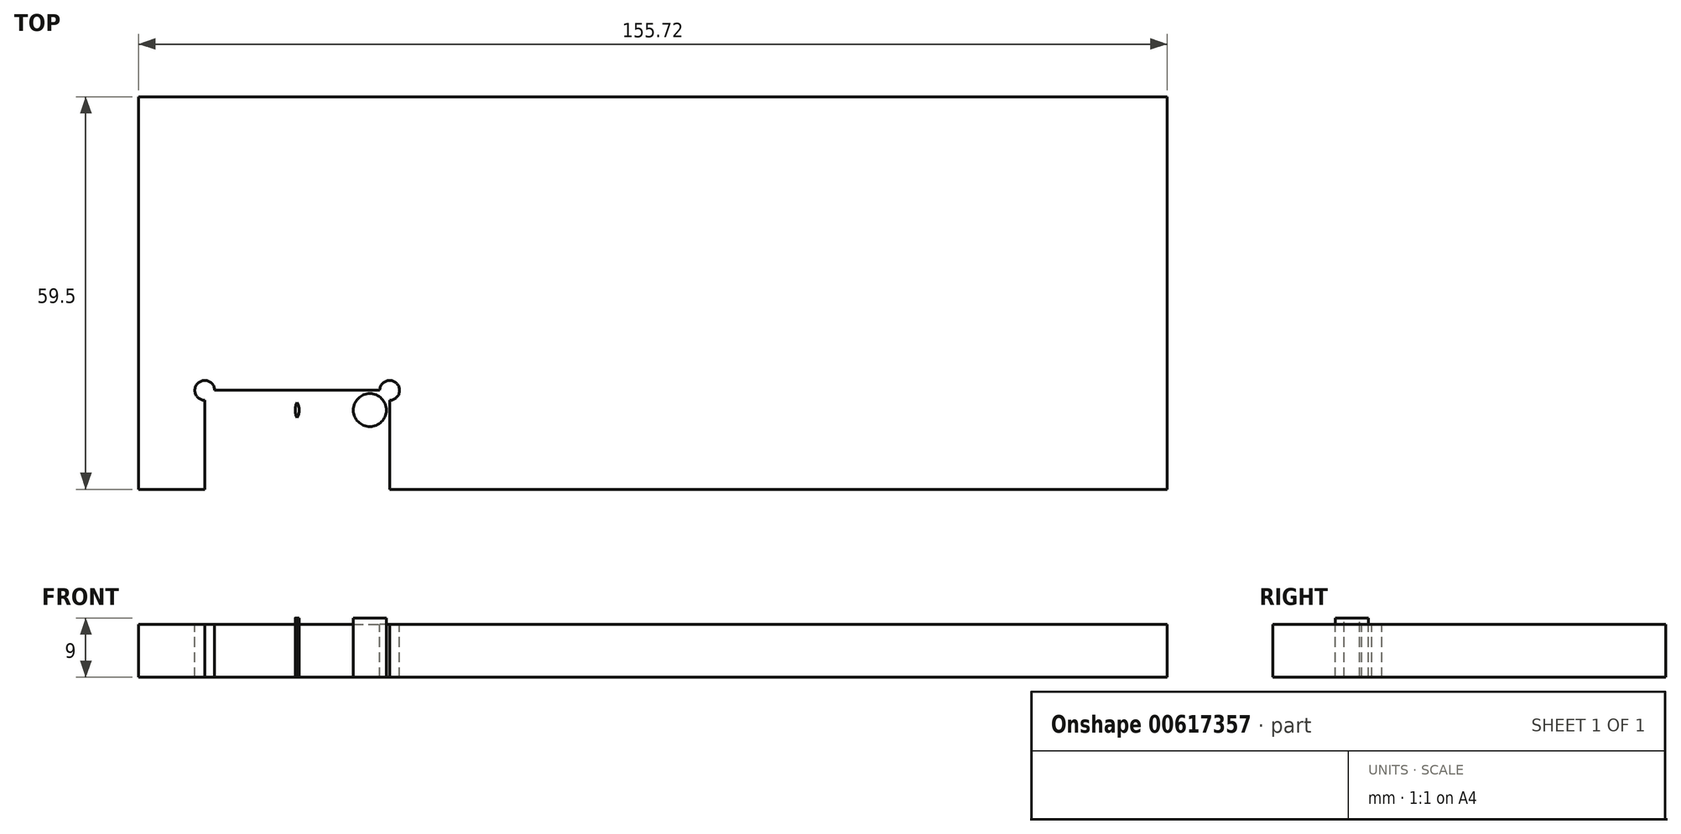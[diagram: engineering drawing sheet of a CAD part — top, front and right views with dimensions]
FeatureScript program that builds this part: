
annotation { "Feature Type Name" : "Feature", "Feature Type Description" : "" }
export const myFeature = defineFeature(function(context is Context, id is Id, definition is map)
    precondition{}
    {
        {
            var Q0;
            Q0=qCreatedBy(makeId("Top.planeOp"),FACE);
            var sketch = newSketch(context, id + "F0", { "sketchPlane" : qUnion([Q0])});
            skLineSegment(sketch, "E0.bottom", {"start": v(77.86, 29.75) * mm, "end": v(-77.86, 29.75) * mm});
            skLineSegment(sketch, "E0.top", {"start": v(77.86, -29.75) * mm, "end": v(-39.86, -29.75) * mm});
            skLineSegment(sketch, "E0.left", {"start": v(77.86, 29.75) * mm, "end": v(77.86, -29.75) * mm});
            skLineSegment(sketch, "E0.right", {"start": v(-77.86, 29.75) * mm, "end": v(-77.86, -29.75) * mm});
            skPoint(sketch, "E0.middle", {"position": v(0, 0) * mm});
            skLineSegment(sketch, "E1", {"start": v(-67.86, -29.75) * mm, "end": v(-67.86, -16.25) * mm});
            skLineSegment(sketch, "E2", {"start": v(-66.36, -14.75) * mm, "end": v(-41.36, -14.75) * mm});
            skLineSegment(sketch, "E3", {"start": v(-39.86, -16.25) * mm, "end": v(-39.86, -29.75) * mm});
            skArc(sketch, "E4", {"start": v(-39.86, -16.25) * mm, "mid": v(-38.8, -13.69) * mm, "end": v(-41.36, -14.75) * mm});
            skArc(sketch, "E5", {"start": v(-66.36, -14.75) * mm, "mid": v(-68.92, -13.69) * mm, "end": v(-67.86, -16.25) * mm});
            skLineSegment(sketch, "E6.trimOffspring", {"start": v(-67.86, -29.75) * mm, "end": v(-77.86, -29.75) * mm});
            skLineSegment(sketch, "E7", {"start": v(-67.86, -29.75) * mm, "end": v(-39.86, -29.75) * mm});
            skSolve(sketch);
        }
        {
            var Q0;
            Q0=makeQuery(id+"F0.imprint","IMPRINT",FACE,{"disambiguationData":[TD([[makeQuery(id+"F0.imprint","IMPRINT",EDGE,{"derivedFrom":sQuery(id+"F0.wireOp",EDGE,"E0.bottom")}),1.0]])]});
            var Q1;
            Q1=makeQuery(id+"F0.imprint","IMPRINT",FACE,{"disambiguationData":[TD([[makeQuery(id+"F0.imprint","IMPRINT",EDGE,{"derivedFrom":sQuery(id+"F0.wireOp",EDGE,"E1")}),-1.0]])]});
            extrude(context, id + "F1", {"entities" : qUnion([Q0, Q1]), "depth" : 8 * mm, "offsetDistance" : 25 * mm});
        }
        {
            var Q0;
            Q0=makeQuery(id+"F1.opExtrude","CAP_FACE",FACE,{"disambiguationData":[OSD([sQuery(id+"F0.wireOp",EDGE,"E0.bottom"),sQuery(id+"F0.wireOp",EDGE,"E0.top"),sQuery(id+"F0.wireOp",EDGE,"E0.left"),sQuery(id+"F0.wireOp",EDGE,"E0.right"),sQuery(id+"F0.wireOp",EDGE,"E6.trimOffspring"),sQuery(id+"F0.wireOp",EDGE,"E7")])],"isStart":false});
            var sketch = newSketch(context, id + "F2", { "sketchPlane" : qUnion([Q0])});
            skLineSegment(sketch, "E8", {"start": v(-67.86, -29.75) * mm, "end": v(-67.86, -16.25) * mm});
            skLineSegment(sketch, "E9", {"start": v(-66.36, -14.75) * mm, "end": v(-41.36, -14.75) * mm});
            skLineSegment(sketch, "E10", {"start": v(-39.86, -16.25) * mm, "end": v(-39.86, -29.75) * mm});
            skArc(sketch, "E11", {"start": v(-39.86, -16.25) * mm, "mid": v(-38.8, -13.69) * mm, "end": v(-41.36, -14.75) * mm});
            skArc(sketch, "E12", {"start": v(-66.36, -14.75) * mm, "mid": v(-68.92, -13.69) * mm, "end": v(-67.86, -16.25) * mm});
            skSolve(sketch);
        }
        {
            var Q0;
            Q0 = qSketchRegion(id + "F2", true);
            var Q1;
            {var subQ0=sQuery(id+"F2.wireOp",EDGE,"E8");Q1=makeQuery(id+"F2.imprint","IMPRINT",FACE,{"disambiguationData":[TD([[makeQuery(id+"F2.imprint","IMPRINT",EDGE,{"derivedFrom":subQ0}),-1.0]])]});}
            extrude(context, id + "F3", {"entities" : qUnion([Q0, Q1]), "operationType" : NewBodyOperationType.ADD, "depth" : 1 * mm, "offsetDistance" : 25 * mm});
        }
        {
            var Q0;
            Q0=makeQuery(id+"F3.opExtrude","CAP_FACE",FACE,{"disambiguationData":[OSD([sQuery(id+"F0.wireOp",EDGE,"E0.top"),sQuery(id+"F0.wireOp",EDGE,"E6.trimOffspring"),sQuery(id+"F0.wireOp",EDGE,"E7"),sQuery(id+"F2.wireOp",EDGE,"E8"),sQuery(id+"F2.wireOp",EDGE,"E9"),sQuery(id+"F2.wireOp",EDGE,"E10"),sQuery(id+"F2.wireOp",EDGE,"E11"),sQuery(id+"F2.wireOp",EDGE,"E12")])],"isStart":false});
            var sketch = newSketch(context, id + "F4", { "sketchPlane" : qUnion([Q0])});
            skCircle(sketch, "E13", {"center": v(-64.86, -17.75) * mm, "radius": 2.5 * mm});
            skLineSegment(sketch, "E14", {"start": v(-53.86, 3.66) * mm, "end": v(-53.86, -39.31) * mm});
            skCircle(sketch, "E15", {"center": v(-42.86, -17.75) * mm, "radius": 2.5 * mm});
            skCircle(sketch, "E16.1.0.0", {"center": v(-60.46, -17.75) * mm, "radius": 2.5 * mm});
            skCircle(sketch, "E16.2.0.0", {"center": v(-56.06, -17.75) * mm, "radius": 2.5 * mm});
            skCircle(sketch, "E16.3.0.0", {"center": v(-51.66, -17.75) * mm, "radius": 2.5 * mm});
            skCircle(sketch, "E16.4.0.0", {"center": v(-47.26, -17.75) * mm, "radius": 2.5 * mm});
            skLineSegment(sketch, "E16.direction1", {"start": v(-64.86, -17.75) * mm, "end": v(-60.46, -17.75) * mm, "construction": true});
            skCircle(sketch, "E17", {"center": v(-67.86, -14.75) * mm, "radius": 1.5 * mm});
            skCircle(sketch, "E18", {"center": v(-39.86, -14.75) * mm, "radius": 1.5 * mm});
            skSolve(sketch);
        }
        {
            var Q0;
            {var subQ0=sQuery(id+"F4.wireOp",EDGE,"E16.1.0.0");var subQ1=sQuery(id+"F4.wireOp",EDGE,"E13");var subQ2=makeQuery(id+"F4.imprint","INTERSECT",VERTEX,{"disambiguationData":[OD(0.0)],"derivedFrom":[subQ1,subQ0]});Q0=makeQuery(id+"F4.imprint","IMPRINT",FACE,{"disambiguationData":[TD([[makeQuery(id+"F4.imprint","IMPRINT",EDGE,{"disambiguationData":[TD([[subQ2,-1.0]])],"derivedFrom":subQ1}),1.0]])]});}
            var Q1;
            {var subQ0=sQuery(id+"F4.wireOp",EDGE,"E16.1.0.0");var subQ1=sQuery(id+"F4.wireOp",EDGE,"E13");var subQ2=makeQuery(id+"F4.imprint","INTERSECT",VERTEX,{"disambiguationData":[OD(0.0)],"derivedFrom":[subQ1,subQ0]});Q1=makeQuery(id+"F4.imprint","IMPRINT",FACE,{"disambiguationData":[TD([[makeQuery(id+"F4.imprint","IMPRINT",EDGE,{"disambiguationData":[TD([[subQ2,1.0]])],"derivedFrom":subQ1}),-1.0]])]});}
            var Q2;
            {var subQ0=sQuery(id+"F4.wireOp",EDGE,"E16.2.0.0");var subQ1=sQuery(id+"F4.wireOp",EDGE,"E16.1.0.0");var subQ2=makeQuery(id+"F4.imprint","INTERSECT",VERTEX,{"disambiguationData":[OD(0.0)],"derivedFrom":[subQ1,subQ0]});Q2=makeQuery(id+"F4.imprint","IMPRINT",FACE,{"disambiguationData":[TD([[makeQuery(id+"F4.imprint","IMPRINT",EDGE,{"disambiguationData":[TD([[subQ2,1.0]])],"derivedFrom":subQ1}),-1.0]])]});}
            var Q3;
            {var subQ0=sQuery(id+"F4.wireOp",EDGE,"E16.3.0.0");var subQ5=sQuery(id+"F4.wireOp",EDGE,"E16.4.0.0");var subQ6=makeQuery(id+"F4.imprint","INTERSECT",VERTEX,{"disambiguationData":[OD(0.0)],"derivedFrom":[subQ0,subQ5]});Q3=makeQuery(id+"F4.imprint","IMPRINT",FACE,{"disambiguationData":[TD([[makeQuery(id+"F4.imprint","IMPRINT",EDGE,{"disambiguationData":[TD([[subQ6,-1.0]])],"derivedFrom":subQ5}),-1.0]])]});}
            var Q4;
            {var subQ0=sQuery(id+"F4.wireOp",EDGE,"E16.4.0.0");var subQ1=sQuery(id+"F4.wireOp",EDGE,"E16.3.0.0");var subQ2=makeQuery(id+"F4.imprint","INTERSECT",VERTEX,{"disambiguationData":[OD(0.0)],"derivedFrom":[subQ1,subQ0]});Q4=makeQuery(id+"F4.imprint","IMPRINT",FACE,{"disambiguationData":[TD([[makeQuery(id+"F4.imprint","IMPRINT",EDGE,{"disambiguationData":[TD([[subQ2,1.0]])],"derivedFrom":subQ1}),-1.0]])]});}
            var Q5;
            {var subQ0=sQuery(id+"F4.wireOp",EDGE,"E15");var subQ1=sQuery(id+"F4.wireOp",EDGE,"E16.4.0.0");var subQ2=makeQuery(id+"F4.imprint","INTERSECT",VERTEX,{"disambiguationData":[OD(0.0)],"derivedFrom":[subQ1,subQ0]});Q5=makeQuery(id+"F4.imprint","IMPRINT",FACE,{"disambiguationData":[TD([[makeQuery(id+"F4.imprint","IMPRINT",EDGE,{"disambiguationData":[TD([[subQ2,1.0]])],"derivedFrom":subQ1}),-1.0]])]});}
            var Q6;
            {var subQ0=sQuery(id+"F4.wireOp",EDGE,"E16.2.0.0");var subQ1=sQuery(id+"F4.wireOp",EDGE,"E16.1.0.0");var subQ2=makeQuery(id+"F4.imprint","INTERSECT",VERTEX,{"disambiguationData":[OD(0.0)],"derivedFrom":[subQ1,subQ0]});Q6=makeQuery(id+"F4.imprint","IMPRINT",FACE,{"disambiguationData":[TD([[makeQuery(id+"F4.imprint","IMPRINT",EDGE,{"disambiguationData":[TD([[subQ2,1.0]])],"derivedFrom":subQ1}),1.0]])]});}
            var Q7;
            {var subQ0=sQuery(id+"F4.wireOp",EDGE,"E16.1.0.0");var subQ1=sQuery(id+"F4.wireOp",EDGE,"E13");var subQ2=makeQuery(id+"F4.imprint","INTERSECT",VERTEX,{"disambiguationData":[OD(0.0)],"derivedFrom":[subQ1,subQ0]});Q7=makeQuery(id+"F4.imprint","IMPRINT",FACE,{"disambiguationData":[TD([[makeQuery(id+"F4.imprint","IMPRINT",EDGE,{"disambiguationData":[TD([[subQ2,1.0]])],"derivedFrom":subQ1}),1.0]])]});}
            var Q8;
            {var subQ0=sQuery(id+"F4.wireOp",EDGE,"E16.3.0.0");var subQ1=sQuery(id+"F4.wireOp",EDGE,"E16.2.0.0");var subQ2=sQuery(id+"F4.wireOp",EDGE,"E14");var subQ3=makeQuery(id+"F4.imprint","INTERSECT",VERTEX,{"disambiguationData":[OD(0.0)],"derivedFrom":[subQ2,subQ1,subQ0]});Q8=makeQuery(id+"F4.imprint","IMPRINT",FACE,{"disambiguationData":[TD([[makeQuery(id+"F4.imprint","IMPRINT",EDGE,{"disambiguationData":[TD([[subQ3,-1.0]])],"derivedFrom":subQ2}),1.0]])]});}
            var Q9;
            {var subQ0=sQuery(id+"F4.wireOp",EDGE,"E16.4.0.0");var subQ1=sQuery(id+"F4.wireOp",EDGE,"E16.3.0.0");var subQ2=makeQuery(id+"F4.imprint","INTERSECT",VERTEX,{"disambiguationData":[OD(0.0)],"derivedFrom":[subQ1,subQ0]});Q9=makeQuery(id+"F4.imprint","IMPRINT",FACE,{"disambiguationData":[TD([[makeQuery(id+"F4.imprint","IMPRINT",EDGE,{"disambiguationData":[TD([[subQ2,1.0]])],"derivedFrom":subQ1}),1.0]])]});}
            var Q10;
            {var subQ0=sQuery(id+"F4.wireOp",EDGE,"E15");var subQ1=sQuery(id+"F4.wireOp",EDGE,"E16.4.0.0");var subQ2=makeQuery(id+"F4.imprint","INTERSECT",VERTEX,{"disambiguationData":[OD(0.0)],"derivedFrom":[subQ1,subQ0]});Q10=makeQuery(id+"F4.imprint","IMPRINT",FACE,{"disambiguationData":[TD([[makeQuery(id+"F4.imprint","IMPRINT",EDGE,{"disambiguationData":[TD([[subQ2,1.0]])],"derivedFrom":subQ1}),1.0]])]});}
            var Q11;
            {var subQ0=sQuery(id+"F4.wireOp",EDGE,"E16.3.0.0");var subQ1=sQuery(id+"F4.wireOp",EDGE,"E16.2.0.0");var subQ2=sQuery(id+"F4.wireOp",EDGE,"E14");var subQ3=makeQuery(id+"F4.imprint","INTERSECT",VERTEX,{"disambiguationData":[OD(0.0)],"derivedFrom":[subQ2,subQ1,subQ0]});Q11=makeQuery(id+"F4.imprint","IMPRINT",FACE,{"disambiguationData":[TD([[makeQuery(id+"F4.imprint","IMPRINT",EDGE,{"disambiguationData":[TD([[subQ3,-1.0]])],"derivedFrom":subQ2}),-1.0]])]});}
            var Q12;
            {var subQ0=sQuery(id+"F4.wireOp",EDGE,"E17");var subQ1=makeQuery(id+"F4.imprint","INTERSECT",VERTEX,{"derivedFrom":[makeQuery(id+"F3.opExtrude","CAP_EDGE",EDGE,{"disambiguationData":[OSD([sQuery(id+"F2.wireOp",EDGE,"E8")])],"isStart":false}),subQ0]});Q12=makeQuery(id+"F4.imprint","IMPRINT",FACE,{"disambiguationData":[TD([[makeQuery(id+"F4.imprint","IMPRINT",EDGE,{"disambiguationData":[TD([[subQ1,1.0]])],"derivedFrom":subQ0}),1.0]])]});}
            var Q13;
            {var subQ0=sQuery(id+"F4.wireOp",EDGE,"E18");var subQ1=makeQuery(id+"F4.imprint","INTERSECT",VERTEX,{"derivedFrom":[makeQuery(id+"F3.opExtrude","CAP_EDGE",EDGE,{"disambiguationData":[OSD([sQuery(id+"F2.wireOp",EDGE,"E9")])],"isStart":false}),subQ0]});Q13=makeQuery(id+"F4.imprint","IMPRINT",FACE,{"disambiguationData":[TD([[makeQuery(id+"F4.imprint","IMPRINT",EDGE,{"disambiguationData":[TD([[subQ1,1.0]])],"derivedFrom":subQ0}),1.0]])]});}
            extrude(context, id + "F5", {"entities" : qUnion([Q0, Q1, Q2, Q3, Q4, Q5, Q6, Q7, Q8, Q9, Q10, Q11, Q12, Q13]), "operationType" : NewBodyOperationType.REMOVE, "oppositeDirection" : true, "depth" : 25 * mm, "offsetDistance" : 25 * mm});
        }
    });
